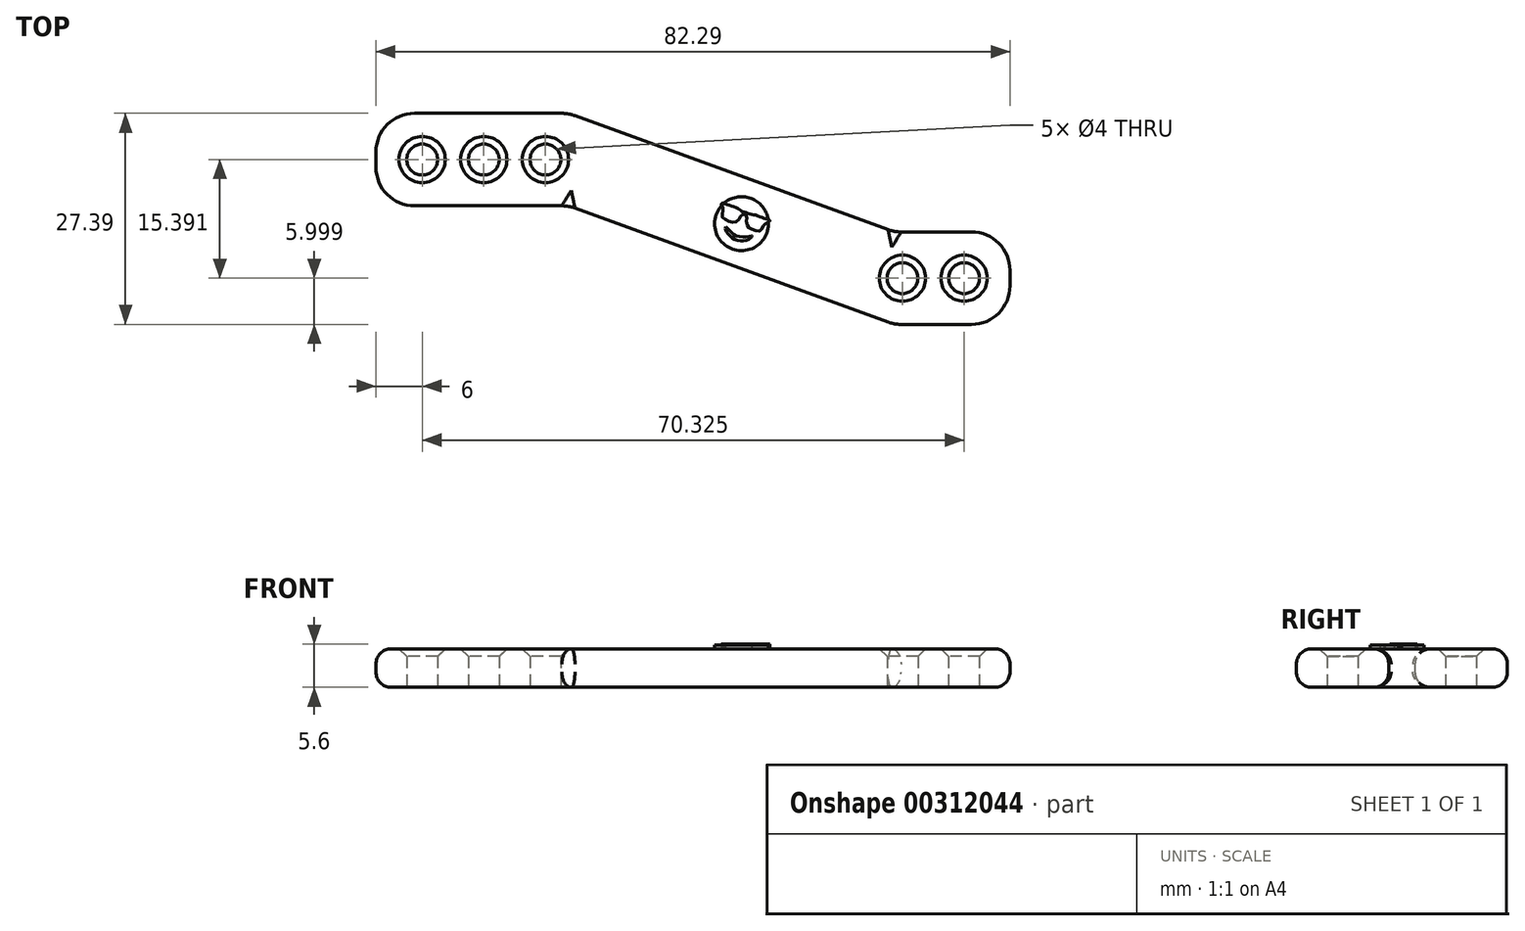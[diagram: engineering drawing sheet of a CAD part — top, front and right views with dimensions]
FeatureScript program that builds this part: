
annotation { "Feature Type Name" : "Feature", "Feature Type Description" : "" }
export const myFeature = defineFeature(function(context is Context, id is Id, definition is map)
    precondition{}
    {
        {
            var Q0;
            Q0=qCreatedBy(makeId("Top.planeOp"),FACE);
            var sketch = newSketch(context, id + "F0", { "sketchPlane" : qUnion([Q0])});
            skLineSegment(sketch, "E0.bottom", {"start": v(0, 0) * mm, "end": v(25, 0) * mm});
            skLineSegment(sketch, "E0.top", {"start": v(0, -12) * mm, "end": v(25, -12) * mm});
            skLineSegment(sketch, "E0.left", {"start": v(0, 0) * mm, "end": v(0, -12) * mm});
            skLineSegment(sketch, "E0.right", {"start": v(25, 0) * mm, "end": v(25, -12) * mm});
            skLineSegment(sketch, "E1.bottom", {"start": v(82.29, -27.4) * mm, "end": v(67.29, -27.4) * mm});
            skLineSegment(sketch, "E1.top", {"start": v(82.29, -15.4) * mm, "end": v(67.29, -15.4) * mm});
            skLineSegment(sketch, "E1.left", {"start": v(82.29, -27.4) * mm, "end": v(82.29, -15.4) * mm});
            skLineSegment(sketch, "E1.right", {"start": v(67.29, -27.4) * mm, "end": v(67.29, -15.4) * mm});
            skLineSegment(sketch, "E2", {"start": v(25, -12) * mm, "end": v(67.29, -27.4) * mm});
            skLineSegment(sketch, "E3", {"start": v(25, 0) * mm, "end": v(67.29, -15.4) * mm});
            skSolve(sketch);
        }
        {
            var Q0;
            Q0 = qSketchRegion(id + "F0", true);
            extrude(context, id + "F1", {"entities" : qUnion([Q0]), "depth" : 5 * mm});
        }
        {
            var Q0;
            Q0 = qSketchRegion(id + "F0", true);
            var sketch = newSketch(context, id + "F2", { "sketchPlane" : qUnion([Q0])});
            skCircle(sketch, "E4", {"center": v(6, -6) * mm, "radius": 2 * mm});
            skPoint(sketch, "E5", {"position": v(0, -6) * mm});
            skCircle(sketch, "E6.1.0.0", {"center": v(14, -6) * mm, "radius": 2 * mm});
            skCircle(sketch, "E6.2.0.0", {"center": v(22, -6) * mm, "radius": 2 * mm});
            skLineSegment(sketch, "E6.direction1", {"start": v(6, -6) * mm, "end": v(14, -6) * mm, "construction": true});
            skCircle(sketch, "E7", {"center": v(76.33, -21.4) * mm, "radius": 2 * mm});
            skPoint(sketch, "E8", {"position": v(82.33, -21.4) * mm});
            skCircle(sketch, "E9.1.0.0", {"center": v(68.33, -21.4) * mm, "radius": 2 * mm});
            skLineSegment(sketch, "E9.direction1", {"start": v(76.33, -21.4) * mm, "end": v(68.33, -21.4) * mm, "construction": true});
            skSolve(sketch);
        }
        {
            var Q0;
            Q0 = qSketchRegion(id + "F2", true);
            extrude(context, id + "F3", {"entities" : qUnion([Q0]), "operationType" : NewBodyOperationType.REMOVE, "endBound" : BoundingType.THROUGH_ALL, "depth" : 25 * mm});
        }
        {
            var Q0;
            Q0=makeQuery(id+"F1.opExtrude","CAP_EDGE",EDGE,{"disambiguationData":[OSD([sQuery(id+"F0.wireOp",EDGE,"E0.bottom")])],"isStart":false});
            var Q1;
            Q1=makeQuery(id+"F1.opExtrude","CAP_EDGE",EDGE,{"disambiguationData":[OSD([sQuery(id+"F0.wireOp",EDGE,"E0.left")])],"isStart":false});
            var Q2;
            Q2=makeQuery(id+"F1.opExtrude","CAP_EDGE",EDGE,{"disambiguationData":[OSD([sQuery(id+"F0.wireOp",EDGE,"E3")])],"isStart":false});
            var Q3;
            Q3=makeQuery(id+"F1.opExtrude","CAP_EDGE",EDGE,{"disambiguationData":[OSD([sQuery(id+"F0.wireOp",EDGE,"E1.top")])],"isStart":false});
            var Q4;
            Q4=makeQuery(id+"F1.opExtrude","CAP_EDGE",EDGE,{"disambiguationData":[OSD([sQuery(id+"F0.wireOp",EDGE,"E0.top")])],"isStart":false});
            var Q5;
            Q5=makeQuery(id+"F1.opExtrude","CAP_EDGE",EDGE,{"disambiguationData":[OSD([sQuery(id+"F0.wireOp",EDGE,"E2")])],"isStart":false});
            var Q6;
            Q6=makeQuery(id+"F1.opExtrude","CAP_EDGE",EDGE,{"disambiguationData":[OSD([sQuery(id+"F0.wireOp",EDGE,"E1.bottom")])],"isStart":false});
            var Q7;
            Q7=makeQuery(id+"F1.opExtrude","CAP_EDGE",EDGE,{"disambiguationData":[OSD([sQuery(id+"F0.wireOp",EDGE,"E1.left")])],"isStart":false});
            var Q8;
            Q8=makeQuery(id+"F1.opExtrude","CAP_EDGE",EDGE,{"disambiguationData":[OSD([sQuery(id+"F0.wireOp",EDGE,"E1.left")])],"isStart":true});
            var Q9;
            Q9=makeQuery(id+"F1.opExtrude","CAP_EDGE",EDGE,{"disambiguationData":[OSD([sQuery(id+"F0.wireOp",EDGE,"E1.bottom")])],"isStart":true});
            var Q10;
            Q10=makeQuery(id+"F1.opExtrude","CAP_EDGE",EDGE,{"disambiguationData":[OSD([sQuery(id+"F0.wireOp",EDGE,"E2")])],"isStart":true});
            var Q11;
            Q11=makeQuery(id+"F1.opExtrude","CAP_EDGE",EDGE,{"disambiguationData":[OSD([sQuery(id+"F0.wireOp",EDGE,"E0.top")])],"isStart":true});
            var Q12;
            Q12=makeQuery(id+"F1.opExtrude","CAP_EDGE",EDGE,{"disambiguationData":[OSD([sQuery(id+"F0.wireOp",EDGE,"E0.left")])],"isStart":true});
            var Q13;
            Q13=makeQuery(id+"F1.opExtrude","CAP_EDGE",EDGE,{"disambiguationData":[OSD([sQuery(id+"F0.wireOp",EDGE,"E0.bottom")])],"isStart":true});
            var Q14;
            Q14=makeQuery(id+"F1.opExtrude","CAP_EDGE",EDGE,{"disambiguationData":[OSD([sQuery(id+"F0.wireOp",EDGE,"E3")])],"isStart":true});
            var Q15;
            Q15=makeQuery(id+"F1.opExtrude","CAP_EDGE",EDGE,{"disambiguationData":[OSD([sQuery(id+"F0.wireOp",EDGE,"E1.top")])],"isStart":true});
            fillet(context, id + "F4", {"entities" : qUnion([Q0, Q1, Q2, Q3, Q4, Q5, Q6, Q7, Q8, Q9, Q10, Q11, Q12, Q13, Q14, Q15]), "radius" : 2 * mm, "tangentPropagation" : true, "allowEdgeOverflow" : false});
        }
        {
            var Q0;
            Q0=makeQuery(id+"F1.opExtrude","SWEPT_EDGE",EDGE,{"disambiguationData":[OSD([sQuery(id+"F0.wireOp",EDGE,"E1.bottom"),sQuery(id+"F0.wireOp",EDGE,"E1.left")])]});
            var Q1;
            Q1=makeQuery(id+"F1.opExtrude","SWEPT_EDGE",EDGE,{"disambiguationData":[OSD([sQuery(id+"F0.wireOp",EDGE,"E1.bottom"),sQuery(id+"F0.wireOp",EDGE,"E1.right"),sQuery(id+"F0.wireOp",EDGE,"E2")])]});
            var Q2;
            Q2=makeQuery(id+"F1.opExtrude","SWEPT_EDGE",EDGE,{"disambiguationData":[OSD([sQuery(id+"F0.wireOp",EDGE,"E0.top"),sQuery(id+"F0.wireOp",EDGE,"E0.right"),sQuery(id+"F0.wireOp",EDGE,"E2")])]});
            var Q3;
            Q3=makeQuery(id+"F1.opExtrude","SWEPT_EDGE",EDGE,{"disambiguationData":[OSD([sQuery(id+"F0.wireOp",EDGE,"E0.top"),sQuery(id+"F0.wireOp",EDGE,"E0.left")])]});
            var Q4;
            Q4=makeQuery(id+"F1.opExtrude","SWEPT_EDGE",EDGE,{"disambiguationData":[OSD([sQuery(id+"F0.wireOp",EDGE,"E0.bottom"),sQuery(id+"F0.wireOp",EDGE,"E0.left")])]});
            var Q5;
            Q5=makeQuery(id+"F1.opExtrude","SWEPT_EDGE",EDGE,{"disambiguationData":[OSD([sQuery(id+"F0.wireOp",EDGE,"E0.bottom"),sQuery(id+"F0.wireOp",EDGE,"E0.right"),sQuery(id+"F0.wireOp",EDGE,"E3")])]});
            var Q6;
            Q6=makeQuery(id+"F1.opExtrude","SWEPT_EDGE",EDGE,{"disambiguationData":[OSD([sQuery(id+"F0.wireOp",EDGE,"E1.top"),sQuery(id+"F0.wireOp",EDGE,"E1.right"),sQuery(id+"F0.wireOp",EDGE,"E3")])]});
            var Q7;
            Q7=makeQuery(id+"F1.opExtrude","SWEPT_EDGE",EDGE,{"disambiguationData":[OSD([sQuery(id+"F0.wireOp",EDGE,"E1.top"),sQuery(id+"F0.wireOp",EDGE,"E1.left")])]});
            fillet(context, id + "F5", {"entities" : qUnion([Q0, Q1, Q2, Q3, Q4, Q5, Q6, Q7]), "radius" : 5 * mm, "tangentPropagation" : true, "allowEdgeOverflow" : false});
        }
        {
            var Q0;
            Q0=makeQuery(id+"F3.boolean.opBoolean","INTERSECT",EDGE,{"derivedFrom":[makeQuery(id+"F1.opExtrude","CAP_FACE",FACE,{"disambiguationData":[OSD([sQuery(id+"F0.wireOp",EDGE,"E0.bottom"),sQuery(id+"F0.wireOp",EDGE,"E0.top"),sQuery(id+"F0.wireOp",EDGE,"E0.left"),sQuery(id+"F0.wireOp",EDGE,"E1.bottom"),sQuery(id+"F0.wireOp",EDGE,"E1.top"),sQuery(id+"F0.wireOp",EDGE,"E1.left"),sQuery(id+"F0.wireOp",EDGE,"E2"),sQuery(id+"F0.wireOp",EDGE,"E3")])],"isStart":false}),makeQuery(id+"F3.opExtrude","SWEPT_FACE",FACE,{"disambiguationData":[OSD([sQuery(id+"F2.wireOp",EDGE,"E4")])]})]});
            var Q1;
            Q1=makeQuery(id+"F3.boolean.opBoolean","INTERSECT",EDGE,{"derivedFrom":[makeQuery(id+"F1.opExtrude","CAP_FACE",FACE,{"disambiguationData":[OSD([sQuery(id+"F0.wireOp",EDGE,"E0.bottom"),sQuery(id+"F0.wireOp",EDGE,"E0.top"),sQuery(id+"F0.wireOp",EDGE,"E0.left"),sQuery(id+"F0.wireOp",EDGE,"E1.bottom"),sQuery(id+"F0.wireOp",EDGE,"E1.top"),sQuery(id+"F0.wireOp",EDGE,"E1.left"),sQuery(id+"F0.wireOp",EDGE,"E2"),sQuery(id+"F0.wireOp",EDGE,"E3")])],"isStart":false}),makeQuery(id+"F3.opExtrude","SWEPT_FACE",FACE,{"disambiguationData":[OSD([sQuery(id+"F2.wireOp",EDGE,"E6.1.0.0")])]})]});
            var Q2;
            Q2=makeQuery(id+"F3.boolean.opBoolean","INTERSECT",EDGE,{"derivedFrom":[makeQuery(id+"F1.opExtrude","CAP_FACE",FACE,{"disambiguationData":[OSD([sQuery(id+"F0.wireOp",EDGE,"E0.bottom"),sQuery(id+"F0.wireOp",EDGE,"E0.top"),sQuery(id+"F0.wireOp",EDGE,"E0.left"),sQuery(id+"F0.wireOp",EDGE,"E1.bottom"),sQuery(id+"F0.wireOp",EDGE,"E1.top"),sQuery(id+"F0.wireOp",EDGE,"E1.left"),sQuery(id+"F0.wireOp",EDGE,"E2"),sQuery(id+"F0.wireOp",EDGE,"E3")])],"isStart":false}),makeQuery(id+"F3.opExtrude","SWEPT_FACE",FACE,{"disambiguationData":[OSD([sQuery(id+"F2.wireOp",EDGE,"E6.2.0.0")])]})]});
            var Q3;
            Q3=makeQuery(id+"F3.boolean.opBoolean","INTERSECT",EDGE,{"derivedFrom":[makeQuery(id+"F1.opExtrude","CAP_FACE",FACE,{"disambiguationData":[OSD([sQuery(id+"F0.wireOp",EDGE,"E0.bottom"),sQuery(id+"F0.wireOp",EDGE,"E0.top"),sQuery(id+"F0.wireOp",EDGE,"E0.left"),sQuery(id+"F0.wireOp",EDGE,"E1.bottom"),sQuery(id+"F0.wireOp",EDGE,"E1.top"),sQuery(id+"F0.wireOp",EDGE,"E1.left"),sQuery(id+"F0.wireOp",EDGE,"E2"),sQuery(id+"F0.wireOp",EDGE,"E3")])],"isStart":false}),makeQuery(id+"F3.opExtrude","SWEPT_FACE",FACE,{"disambiguationData":[OSD([sQuery(id+"F2.wireOp",EDGE,"E9.1.0.0")])]})]});
            var Q4;
            Q4=makeQuery(id+"F3.boolean.opBoolean","INTERSECT",EDGE,{"derivedFrom":[makeQuery(id+"F1.opExtrude","CAP_FACE",FACE,{"disambiguationData":[OSD([sQuery(id+"F0.wireOp",EDGE,"E0.bottom"),sQuery(id+"F0.wireOp",EDGE,"E0.top"),sQuery(id+"F0.wireOp",EDGE,"E0.left"),sQuery(id+"F0.wireOp",EDGE,"E1.bottom"),sQuery(id+"F0.wireOp",EDGE,"E1.top"),sQuery(id+"F0.wireOp",EDGE,"E1.left"),sQuery(id+"F0.wireOp",EDGE,"E2"),sQuery(id+"F0.wireOp",EDGE,"E3")])],"isStart":false}),makeQuery(id+"F3.opExtrude","SWEPT_FACE",FACE,{"disambiguationData":[OSD([sQuery(id+"F2.wireOp",EDGE,"E7")])]})]});
            chamfer(context, id + "F6", {"entities" : qUnion([Q0, Q1, Q2, Q3, Q4]), "width" : 1 * mm, "tangentPropagation" : true});
        }
        {
            var Q0;
            Q0=makeQuery(id+"F1.opExtrude","CAP_FACE",FACE,{"disambiguationData":[OSD([sQuery(id+"F0.wireOp",EDGE,"E0.bottom"),sQuery(id+"F0.wireOp",EDGE,"E0.top"),sQuery(id+"F0.wireOp",EDGE,"E0.left"),sQuery(id+"F0.wireOp",EDGE,"E1.bottom"),sQuery(id+"F0.wireOp",EDGE,"E1.top"),sQuery(id+"F0.wireOp",EDGE,"E1.left"),sQuery(id+"F0.wireOp",EDGE,"E2"),sQuery(id+"F0.wireOp",EDGE,"E3")])],"isStart":false});
            var sketch = newSketch(context, id + "F7", { "sketchPlane" : qUnion([Q0])});
            skArc(sketch, "E10", {"start": v(44.87, -11.95) * mm, "mid": v(46.27, -17.61) * mm, "end": v(50.94, -14.1) * mm});
            skFitSpline(sketch, "E11", {"points": [v(44.89, -11.7) * mm, v(44.82, -11.83) * mm, v(44.92, -12.05) * mm, v(45, -12.17) * mm, v(45.07, -12.26) * mm, v(45.04, -12.51) * mm, v(44.96, -12.86) * mm, v(44.96, -13.2) * mm, v(44.97, -13.47) * mm, v(45.1, -13.66) * mm, v(45.46, -13.84) * mm, v(45.82, -14) * mm, v(46.17, -14.12) * mm, v(46.54, -14.17) * mm, v(46.92, -14.02) * mm, v(47.15, -13.75) * mm, v(47.26, -13.5) * mm, v(47.38, -13.3) * mm, v(47.59, -13.14) * mm, v(47.81, -13.16) * mm, v(48.06, -13.24) * mm, v(48.17, -13.48) * mm, v(48.09, -13.84) * mm, v(48.1, -14.13) * mm, v(48.16, -14.46) * mm, v(48.26, -14.7) * mm, v(48.4, -14.88) * mm, v(48.73, -15.02) * mm, v(49.17, -15.16) * mm, v(49.5, -15.27) * mm, v(49.83, -15.27) * mm, v(50, -15.09) * mm, v(50.16, -14.84) * mm, v(50.38, -14.49) * mm, v(50.48, -14.36) * mm, v(50.7, -14.22) * mm, v(50.94, -14.1) * mm, v(51.06, -14.05) * mm, v(51.09, -13.85) * mm, v(50.9, -13.77) * mm, v(50.51, -13.66) * mm, v(50.1, -13.5) * mm, v(49.77, -13.38) * mm, v(49.3, -13.2) * mm, v(49, -13.16) * mm, v(48.62, -13.12) * mm, v(48.32, -13) * mm, v(47.94, -12.86) * mm, v(47.56, -12.73) * mm, v(47.4, -12.67) * mm, v(47.25, -12.53) * mm, v(47.06, -12.36) * mm, v(46.63, -12.19) * mm, v(46.26, -12.06) * mm, v(45.77, -11.9) * mm, v(45.4, -11.76) * mm, v(45.11, -11.7) * mm, v(44.89, -11.7) * mm]});
            skFitSpline(sketch, "E12", {"points": [v(45.37, -14.7) * mm, v(45.32, -14.85) * mm, v(45.38, -15.11) * mm, v(45.58, -15.49) * mm, v(45.76, -15.72) * mm, v(46.05, -16.03) * mm, v(46.27, -16.22) * mm, v(46.62, -16.38) * mm, v(46.98, -16.51) * mm, v(47.28, -16.54) * mm, v(47.63, -16.54) * mm, v(47.99, -16.48) * mm, v(48.27, -16.38) * mm, v(48.58, -16.22) * mm, v(48.76, -16.05) * mm, v(48.78, -15.92) * mm, v(48.66, -15.9) * mm, v(48.2, -16) * mm, v(47.79, -16.02) * mm, v(47.35, -16) * mm, v(46.87, -15.93) * mm, v(46.57, -15.78) * mm, v(46.32, -15.6) * mm, v(46.04, -15.37) * mm, v(45.83, -15.16) * mm, v(45.62, -14.93) * mm, v(45.37, -14.7) * mm]});
            skArc(sketch, "E13.trimOffspring", {"start": v(50.9, -13.77) * mm, "mid": v(48.62, -11.02) * mm, "end": v(45.11, -11.7) * mm});
            skSolve(sketch);
        }
        {
            var Q0;
            {var subQ0=sQuery(id+"F7.wireOp",EDGE,"E11");var subQ1=sQuery(id+"F7.wireOp",EDGE,"E10");var subQ2=makeQuery(id+"F7.imprint","INTERSECT",VERTEX,{"disambiguationData":[OD(0.0)],"derivedFrom":[subQ1,subQ0]});Q0=makeQuery(id+"F7.imprint","IMPRINT",FACE,{"disambiguationData":[TD([[makeQuery(id+"F7.imprint","IMPRINT",EDGE,{"disambiguationData":[TD([[subQ2,-1.0]])],"derivedFrom":subQ0}),1.0]])]});}
            extrude(context, id + "F8", {"entities" : qUnion([Q0]), "operationType" : NewBodyOperationType.ADD, "depth" : 0.6 * mm});
        }
        {
            var Q0;
            {var subQ0=sQuery(id+"F7.wireOp",EDGE,"E13.trimOffspring");Q0=makeQuery(id+"F7.imprint","IMPRINT",FACE,{"disambiguationData":[TD([[makeQuery(id+"F7.imprint","IMPRINT",EDGE,{"derivedFrom":subQ0}),1.0]])]});}
            var Q1;
            Q1=makeQuery(id+"F7.imprint","IMPRINT",FACE,{"disambiguationData":[TD([[makeQuery(id+"F7.imprint","IMPRINT",EDGE,{"derivedFrom":sQuery(id+"F7.wireOp",EDGE,"E12")}),-1.0]])]});
            extrude(context, id + "F9", {"entities" : qUnion([Q0, Q1]), "operationType" : NewBodyOperationType.ADD, "depth" : 0.5 * mm});
        }
    });
